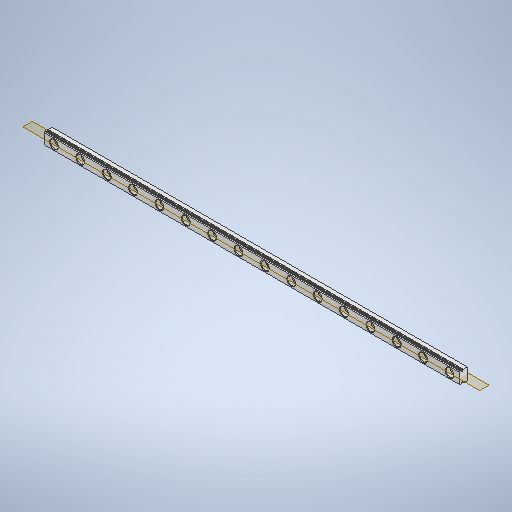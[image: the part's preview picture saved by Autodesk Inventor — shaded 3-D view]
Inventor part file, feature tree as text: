
AUTODESK INVENTOR PART (.ipt)
format: ipt  version: 2025.2 (Build 292293000, 293)  size: 339,968 bytes
history: native  units: in
note: dims shown in document units (in); Inventor stores cm internally (conversion verified against a paired STEP export)
features: plane x2
ambient origin geometry x8: Origin, YZ Plane, XZ Plane, XY Plane, X Axis, Y Axis, Z Axis, Center Point
bodies: Solid1 (feature_tree), Body1 (feature_tree)
feature tree (2):
  plane  "Work Plane2"
  plane  "Work Plane3"
